# Revit family: Festpunkt Typ A Größe II, U-Stahl, Ø 60,3-114,3, V4A
name_source: partatom
category: HLS-Bauteile
revit_build: Autodesk Revit 2017 (Build: 20190507_1515(x64)
units: mm (PartAtom-declared; Revit-internal decimal feet)

## family parameters
Arbeitsebenenbasiert = Ja
Beim Laden mit Abzugskörper schneiden = Nein
Bemaßung runder Anschluss = Durchmesser verwenden
Gemeinsam genutzt = Ja
Immer vertikal = Nein
Raumberechnungspunkt = Nein
Teiletyp = Normal

## types (10) — shared parameters
Anzahl Rohrschellen = 2
Ausführung = mit Schweißnase
Baustoffklasse = B2
Breite Material Rohrschelle = 50 mm
Breite Profilstahl = 65 mm
Fabrikat = MEFA
Firma = MEFA Befestigungs- und Montagesysteme GmbH
Höhe Profilstahl = 42 mm
Klammergröße = 2
Kurztext1 = Festpunkt Typ A V4A
Länge Druckstück = 116 mm
Länge Profilstahl = 200 mm  [stored 0.656168 ft]
Material Druckstücke = Edelstahl
Materialname Druckstücke = V4A
Mengeneinheit = St
Oberfläche Träger + Schellen = galvanisch verzinkt
Profilstahltyp = U65
Rohrschellentyp = Titan HD
Stärke Material Rohrschelle = 5 mm
Vorgabe-Ansicht = 1219 mm
vpe = 1 St
zero-valued in all types: max. Höhe, max. Rohraußendurchmesser, min. Rohraußendurchmesser

## per-type parameters (varying)
| type | Artikelnummer | Aufbaumaß | Breite | Druckstück Typ II | EAN | Gewicht | Gewicht pro Bauteil | Kurztext2 | Material Schalldämmeinlage | RA | Rohraußendurchmesser | Rohrschellen | Schalldämmeinlage | max. Temperaturbeständigkeit |
| Festpunkt Typ A Größe II, Ø 60,3, Gummi, V4A | 9999376 | 43 mm | 148 mm  [stored 0.485564 ft] | Druckstück Typ II Gummi für Edelstahl : Druckstück Typ II Gummi | 4250928447272 | 4.75 kg | 4.75 kg | 60.3 mm Gummi mit Schweißnase | TPE | 72 mm | 60 mm  [stored 0.19685 ft] | MEFA RS Titan HD, Ø60,3-Ø160 mm, TPE : MEFA RS Titan HD, Ø60,3 mm, TPE | Gummi | 100 °C |
| Festpunkt Typ A Größe II, Ø 76,1, Gummi, V4A | 9999377 | 63 mm | 166 mm  [stored 0.544619 ft] | Druckstück Typ II Gummi für Edelstahl : Druckstück Typ II Gummi | 4250928447289 | 4.99 kg | 4.99 kg | 76.1 mm Gummi mit Schweißnase | TPE | 82 mm  [stored 0.269029 ft] | 76 mm  [stored 0.249344 ft] | MEFA RS Titan HD, Ø60,3-Ø160 mm, TPE : MEFA RS Titan HD, Ø76,1mm, TPE | Gummi | 100 °C |
| Festpunkt Typ A Größe II, Ø 88,9, Gummi, V4A | 9999378 | 63 mm | 179 mm  [stored 0.58727 ft] | Druckstück Typ II Gummi für Edelstahl : Druckstück Typ II Gummi | 4250928447296 | 5.20 kg | 5.20 kg | 88.9 mm Gummi mit Schweißnase | TPE | 90 mm  [stored 0.295276 ft] | 89 mm  [stored 0.291995 ft] | MEFA RS Titan HD, Ø60,3-Ø160 mm, TPE : MEFA RS Titan HD, Ø88,9 mm, AG M12, TPE | Gummi | 100 °C |
| Festpunkt Typ A Größe II, Ø108, Gummi, V4A | 9999379 | 63 mm | 198 mm  [stored 0.649606 ft] | Druckstück Typ II Gummi für Edelstahl : Druckstück Typ II Gummi | 4250928447302 | 5.47 kg | 5.47 kg | 108 mm Gummi mit Schweißnase | TPE | 100 mm  [stored 0.328084 ft] | 108 mm  [stored 0.354331 ft] | MEFA RS Titan HD, Ø60,3-Ø160 mm, TPE : MEFA RS Titan HD, Ø108 mm, TPE | Gummi | 100 °C |
| Festpunkt Typ A Größe II, Ø114,3, Gummi, V4A | 9999380 | 63 mm | 204 mm | Druckstück Typ II Gummi für Edelstahl : Druckstück Typ II Gummi | 4250928447319 | 5.56 kg | 5.56 kg | 114.3 mm Gummi mit Schweißnase | TPE | 104 mm | 114 mm  [stored 0.374016 ft] | MEFA RS Titan HD, Ø60,3-Ø160 mm, TPE : MEFA RS Titan HD, Ø114,3 mm, TPE | Gummi | 100 °C |
| Festpunkt Typ A Größe II, Ø 60,3, Silikon, V4A | 9999390 | 43 mm | 148 mm  [stored 0.485564 ft] | Druckstück Typ II Sillikon für Edelstahl : Druckstück Typ II Gummi | 4250928447418 | 4.75 kg | 4.75 kg | 60.3 mm Silikon mit Schweißnase | Silikon | 72 mm | 60 mm  [stored 0.19685 ft] | MEFA RS Titan HD, Ø60,3-Ø160 mm, Silikon : MEFA RS Titan HD, Ø60,3 mm, Silikon | Silikon | 250 °C |
| Festpunkt Typ A Größe II, Ø 76,1, Silikon, V4A | 9999391 | 63 mm | 166 mm  [stored 0.544619 ft] | Druckstück Typ II Sillikon für Edelstahl : Druckstück Typ II Gummi | 4250928447425 | 4.99 kg | 4.99 kg | 76.1 mm Silikon mit Schweißnase | Silikon | 82 mm  [stored 0.269029 ft] | 76 mm  [stored 0.249344 ft] | MEFA RS Titan HD, Ø60,3-Ø160 mm, Silikon : MEFA RS Titan HD, Ø76,1 mm, Silikon | Silikon | 250 °C |
| Festpunkt Typ A Größe II, Ø 88,9, Silikon, V4A | 9999392 | 63 mm | 179 mm  [stored 0.58727 ft] | Druckstück Typ II Sillikon für Edelstahl : Druckstück Typ II Gummi | 4250928447432 | 5.20 kg | 5.20 kg | 88.9 mm Silikon mit Schweißnase | Silikon | 90 mm  [stored 0.295276 ft] | 89 mm  [stored 0.291995 ft] | MEFA RS Titan HD, Ø60,3-Ø160 mm, Silikon : MEFA RS Titan HD, Ø88,9 mm, Silikon | Silikon | 250 °C |
| Festpunkt Typ A Größe II, Ø108, Silikon, V4A | 9999393 | 63 mm | 198 mm  [stored 0.649606 ft] | Druckstück Typ II Sillikon für Edelstahl : Druckstück Typ II Gummi | 4250928447449 | 5.47 kg | 5.47 kg | 108 mm Silikon mit Schweißnase | Silikon | 100 mm  [stored 0.328084 ft] | 108 mm  [stored 0.354331 ft] | MEFA RS Titan HD, Ø60,3-Ø160 mm, Silikon : MEFA RS Titan HD, Ø108 mm, Silikon | Silikon | 250 °C |
| Festpunkt Typ A Größe II, Ø114,3, Silikon, V4A | 9999394 | 63 mm | 204 mm | Druckstück Typ II Sillikon für Edelstahl : Druckstück Typ II Gummi | 4250928447456 | 5.56 kg | 5.56 kg | 114.3 mm Silikon mit Schweißnase | Silikon | 104 mm | 114 mm  [stored 0.374016 ft] | MEFA RS Titan HD, Ø60,3-Ø160 mm, Silikon : MEFA RS Titan HD, Ø114,3 mm, Silikon | Silikon | 250 °C |

note: [stored X ft] marks values corroborated as IEEE doubles in the binary element streams (Revit-internal decimal feet)

## geometry (parser evidence)
native form markers: Sweep x10
no freeform markers — native parametric forms only
